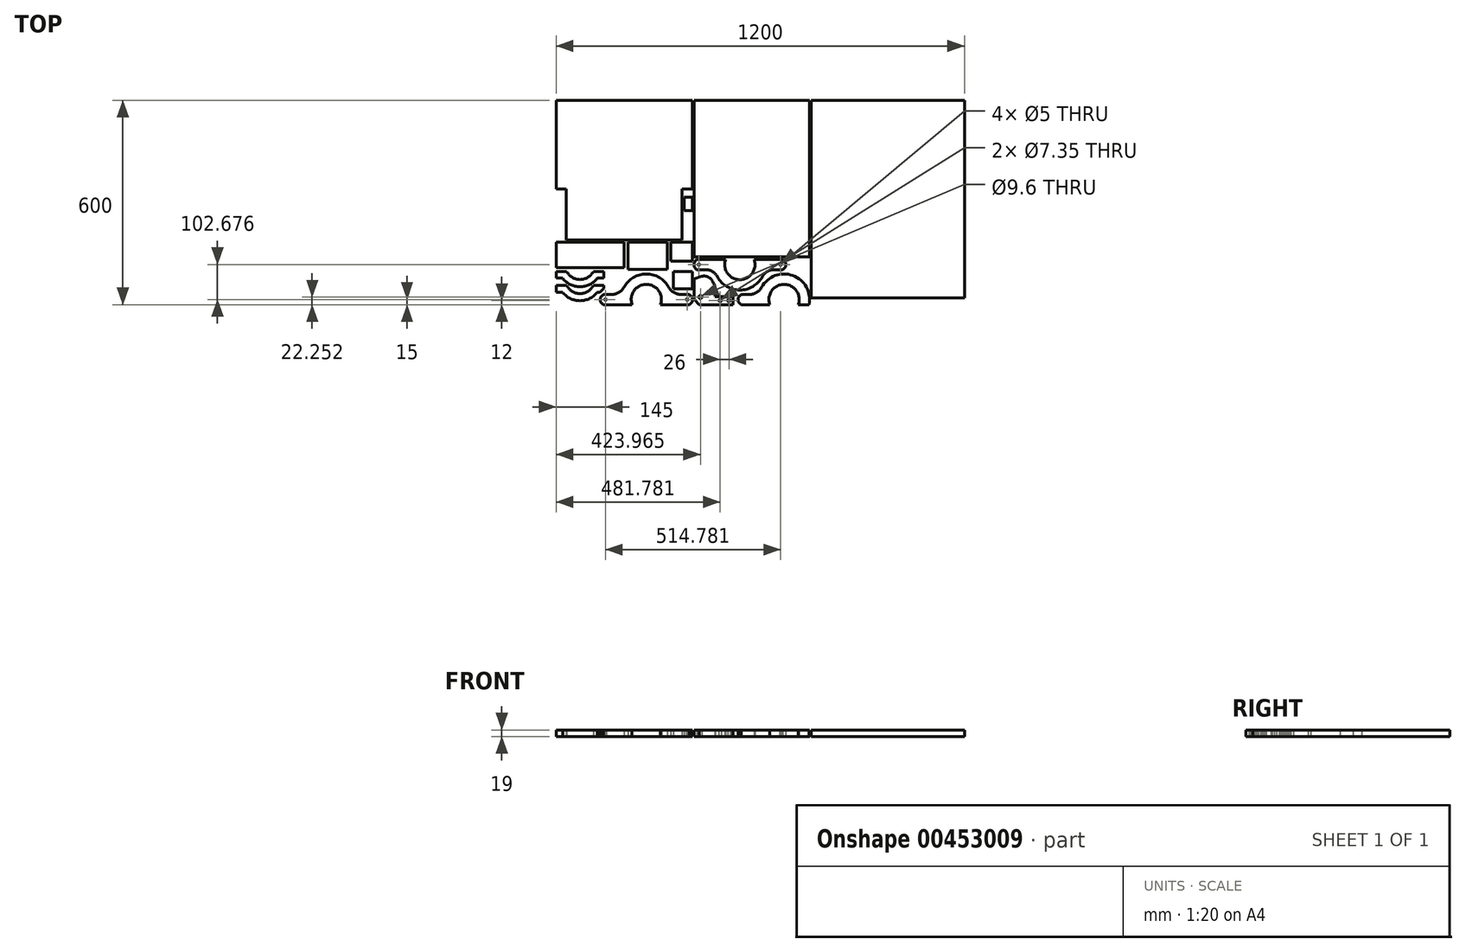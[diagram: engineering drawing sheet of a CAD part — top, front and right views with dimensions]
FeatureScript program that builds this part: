
annotation { "Feature Type Name" : "Feature", "Feature Type Description" : "" }
export const myFeature = defineFeature(function(context is Context, id is Id, definition is map)
    precondition{}
    {
        {
            var Q0;
            Q0=qCreatedBy(makeId("Top.planeOp"),FACE);
            var sketch = newSketch(context, id + "F0", { "sketchPlane" : qUnion([Q0])});
            skLineSegment(sketch, "E0", {"start": v(-600, 40) * mm, "end": v(-570, 40) * mm});
            skLineSegment(sketch, "E1", {"start": v(-570, 40) * mm, "end": v(-570, -110) * mm});
            skLineSegment(sketch, "E2", {"start": v(-570, -110) * mm, "end": v(-230, -110) * mm});
            skLineSegment(sketch, "E3", {"start": v(-230, -110) * mm, "end": v(-230, 40) * mm});
            skLineSegment(sketch, "E4", {"start": v(-230, 40) * mm, "end": v(-200, 40) * mm});
            skLineSegment(sketch, "E5", {"start": v(-200, 40) * mm, "end": v(-200, 300) * mm});
            skLineSegment(sketch, "E6", {"start": v(-200, 300) * mm, "end": v(-600, 300) * mm});
            skLineSegment(sketch, "E7", {"start": v(-600, 300) * mm, "end": v(-600, 40) * mm});
            skLineSegment(sketch, "E8", {"start": v(-400, -110) * mm, "end": v(-400, 300) * mm, "construction": true});
            skLineSegment(sketch, "E9.bottom", {"start": v(-600, 300) * mm, "end": v(600, 300) * mm, "construction": true});
            skLineSegment(sketch, "E9.top", {"start": v(-600, -300) * mm, "end": v(600, -300) * mm, "construction": true});
            skLineSegment(sketch, "E9.left", {"start": v(-600, 300) * mm, "end": v(-600, -300) * mm, "construction": true});
            skLineSegment(sketch, "E9.right", {"start": v(600, 300) * mm, "end": v(600, -300) * mm, "construction": true});
            skPoint(sketch, "E9.middle", {"position": v(0, 0) * mm});
            skLineSegment(sketch, "E10.bottom", {"start": v(-195.22, 300) * mm, "end": v(144.78, 300) * mm});
            skLineSegment(sketch, "E10.top", {"start": v(-195.22, -160) * mm, "end": v(144.78, -160) * mm});
            skLineSegment(sketch, "E10.left", {"start": v(-195.22, 300) * mm, "end": v(-195.22, -160) * mm});
            skLineSegment(sketch, "E10.right", {"start": v(144.78, 300) * mm, "end": v(144.78, -160) * mm});
            skLineSegment(sketch, "E11.bottom", {"start": v(600, 300) * mm, "end": v(150, 300) * mm});
            skLineSegment(sketch, "E11.top", {"start": v(600, -280) * mm, "end": v(150, -280) * mm});
            skLineSegment(sketch, "E11.left", {"start": v(600, 300) * mm, "end": v(600, -280) * mm});
            skLineSegment(sketch, "E11.right", {"start": v(150, 300) * mm, "end": v(150, -280) * mm});
            skSolve(sketch);
        }
        {
            var Q0;
            Q0=qCreatedBy(makeId("Top.planeOp"),FACE);
            var sketch = newSketch(context, id + "F1", { "sketchPlane" : qUnion([Q0])});
            skLineSegment(sketch, "E12.bottom", {"start": v(-600, -116.87) * mm, "end": v(-400, -116.87) * mm});
            skLineSegment(sketch, "E12.top", {"start": v(-600, -191.87) * mm, "end": v(-400, -191.87) * mm});
            skLineSegment(sketch, "E12.left", {"start": v(-600, -116.87) * mm, "end": v(-600, -191.87) * mm});
            skLineSegment(sketch, "E12.right", {"start": v(-400, -116.87) * mm, "end": v(-400, -191.87) * mm});
            skLineSegment(sketch, "E13.bottom", {"start": v(-388.52, -116.87) * mm, "end": v(-273.52, -116.87) * mm});
            skLineSegment(sketch, "E13.top", {"start": v(-388.52, -196.87) * mm, "end": v(-273.52, -196.87) * mm});
            skLineSegment(sketch, "E13.left", {"start": v(-388.52, -116.87) * mm, "end": v(-388.52, -196.87) * mm});
            skLineSegment(sketch, "E13.right", {"start": v(-273.52, -116.87) * mm, "end": v(-273.52, -196.87) * mm});
            skLineSegment(sketch, "E14.bottom", {"start": v(-263, -116.87) * mm, "end": v(-200, -116.87) * mm});
            skLineSegment(sketch, "E14.top", {"start": v(-263, -172.87) * mm, "end": v(-200, -172.87) * mm});
            skLineSegment(sketch, "E14.left", {"start": v(-263, -116.87) * mm, "end": v(-263, -172.87) * mm});
            skLineSegment(sketch, "E14.right", {"start": v(-200, -116.87) * mm, "end": v(-200, -172.87) * mm});
            skLineSegment(sketch, "E15.bottom", {"start": v(-223.55, 15.5) * mm, "end": v(-200, 15.5) * mm});
            skLineSegment(sketch, "E15.top", {"start": v(-223.55, -23.14) * mm, "end": v(-200, -23.14) * mm});
            skLineSegment(sketch, "E15.left", {"start": v(-223.55, 15.5) * mm, "end": v(-223.55, -23.14) * mm});
            skLineSegment(sketch, "E15.right", {"start": v(-200, 15.5) * mm, "end": v(-200, -23.14) * mm});
            skLineSegment(sketch, "E16", {"start": v(-470, -278.79) * mm, "end": v(-470, -291.21) * mm});
            skLineSegment(sketch, "E17", {"start": v(-470, -291.21) * mm, "end": v(-461.21, -300) * mm});
            skLineSegment(sketch, "E18", {"start": v(-461.21, -300) * mm, "end": v(-376.9, -300) * mm});
            skLineSegment(sketch, "E19", {"start": v(-470, -278.79) * mm, "end": v(-461.21, -270) * mm});
            skLineSegment(sketch, "E20", {"start": v(-461.21, -270) * mm, "end": v(-436, -270) * mm});
            skArc(sketch, "E21", {"start": v(-376.9, -300) * mm, "mid": v(-335, -240.5) * mm, "end": v(-293.1, -300) * mm});
            skLineSegment(sketch, "E22", {"start": v(-335, -285) * mm, "end": v(-335, -225.45) * mm, "construction": true});
            skLineSegment(sketch, "E23", {"start": v(-335, -285) * mm, "end": v(-470, -285) * mm, "construction": true});
            skCircle(sketch, "E24", {"center": v(-455, -285) * mm, "radius": 2.5 * mm});
            skArc(sketch, "E25", {"start": v(-436, -270) * mm, "mid": v(-415.57, -264.39) * mm, "end": v(-400.86, -249.13) * mm});
            skArc(sketch, "E26", {"start": v(-335, -210) * mm, "mid": v(-373.3, -220.52) * mm, "end": v(-400.86, -249.13) * mm});
            skLineSegment(sketch, "E27.MirrorCS", {"start": v(-200, -291.21) * mm, "end": v(-208.79, -300) * mm});
            skLineSegment(sketch, "E28.MirrorCS", {"start": v(-200, -278.79) * mm, "end": v(-200, -291.21) * mm});
            skLineSegment(sketch, "E29.MirrorCS", {"start": v(-208.79, -300) * mm, "end": v(-293.1, -300) * mm});
            skArc(sketch, "E30.MirrorCS", {"start": v(-234, -270) * mm, "mid": v(-254.43, -264.39) * mm, "end": v(-269.14, -249.13) * mm});
            skCircle(sketch, "E31.MirrorC", {"center": v(-215, -285) * mm, "radius": 2.5 * mm});
            skLineSegment(sketch, "E32.MirrorCS", {"start": v(-200, -278.79) * mm, "end": v(-208.79, -270) * mm});
            skLineSegment(sketch, "E33.MirrorCS", {"start": v(-208.79, -270) * mm, "end": v(-234, -270) * mm});
            skArc(sketch, "E34.MirrorCS", {"start": v(-335, -210) * mm, "mid": v(-296.7, -220.52) * mm, "end": v(-269.14, -249.13) * mm});
            skLineSegment(sketch, "E35.bottom", {"start": v(-200, -202.36) * mm, "end": v(-256, -202.36) * mm});
            skLineSegment(sketch, "E35.top", {"start": v(-200, -253.36) * mm, "end": v(-256, -253.36) * mm});
            skLineSegment(sketch, "E35.left", {"start": v(-200, -202.36) * mm, "end": v(-200, -253.36) * mm});
            skLineSegment(sketch, "E35.right", {"start": v(-256, -202.36) * mm, "end": v(-256, -253.36) * mm});
            skLineSegment(sketch, "E36", {"start": v(-569.2, -202.36) * mm, "end": v(-600, -202.36) * mm});
            skLineSegment(sketch, "E37", {"start": v(-600, -202.36) * mm, "end": v(-600, -222.36) * mm});
            skLineSegment(sketch, "E38", {"start": v(-600, -222.36) * mm, "end": v(-581.23, -222.36) * mm});
            skArc(sketch, "E39", {"start": v(-569.2, -202.36) * mm, "mid": v(-530, -226.36) * mm, "end": v(-490.8, -202.36) * mm});
            skArc(sketch, "E40", {"start": v(-581.23, -222.36) * mm, "mid": v(-530, -247.36) * mm, "end": v(-478.77, -222.36) * mm});
            skLineSegment(sketch, "E41", {"start": v(-530, -182.36) * mm, "end": v(-530, -247.36) * mm, "construction": true});
            skLineSegment(sketch, "E42.MirrorCS", {"start": v(-460, -222.36) * mm, "end": v(-478.77, -222.36) * mm});
            skLineSegment(sketch, "E43.MirrorCS", {"start": v(-490.8, -202.36) * mm, "end": v(-460, -202.36) * mm});
            skLineSegment(sketch, "E44.MirrorCS", {"start": v(-460, -202.36) * mm, "end": v(-460, -222.36) * mm});
            skLineSegment(sketch, "E45", {"start": v(-569.2, -243.57) * mm, "end": v(-600, -243.57) * mm});
            skLineSegment(sketch, "E46", {"start": v(-600, -243.57) * mm, "end": v(-600, -263.57) * mm});
            skLineSegment(sketch, "E47", {"start": v(-600, -263.57) * mm, "end": v(-581.23, -263.57) * mm});
            skArc(sketch, "E48", {"start": v(-569.2, -243.57) * mm, "mid": v(-530, -267.57) * mm, "end": v(-490.8, -243.57) * mm});
            skArc(sketch, "E49", {"start": v(-581.23, -263.57) * mm, "mid": v(-530, -288.57) * mm, "end": v(-478.77, -263.57) * mm});
            skLineSegment(sketch, "E50", {"start": v(-530, -223.57) * mm, "end": v(-530, -288.57) * mm, "construction": true});
            skLineSegment(sketch, "E51.MirrorCS", {"start": v(-471.72, -263.57) * mm, "end": v(-478.77, -263.57) * mm});
            skLineSegment(sketch, "E52.MirrorCS", {"start": v(-490.8, -243.57) * mm, "end": v(-460, -243.57) * mm});
            skLineSegment(sketch, "E53.MirrorCS", {"start": v(-460, -243.57) * mm, "end": v(-460, -251.85) * mm});
            skLineSegment(sketch, "E54", {"start": v(74.78, -188.54) * mm, "end": v(74.78, -176.11) * mm});
            skLineSegment(sketch, "E55", {"start": v(74.78, -176.11) * mm, "end": v(66, -167.32) * mm});
            skLineSegment(sketch, "E56", {"start": v(66, -167.32) * mm, "end": v(-18.32, -167.32) * mm});
            skLineSegment(sketch, "E57", {"start": v(74.78, -188.54) * mm, "end": v(66, -197.32) * mm});
            skLineSegment(sketch, "E58", {"start": v(66, -197.32) * mm, "end": v(40.78, -197.32) * mm});
            skArc(sketch, "E59", {"start": v(-18.32, -167.32) * mm, "mid": v(-60.22, -226.82) * mm, "end": v(-102.11, -167.32) * mm});
            skLineSegment(sketch, "E60", {"start": v(-60.22, -182.32) * mm, "end": v(-60.22, -241.87) * mm, "construction": true});
            skLineSegment(sketch, "E61", {"start": v(-60.22, -182.32) * mm, "end": v(74.78, -182.32) * mm, "construction": true});
            skCircle(sketch, "E62", {"center": v(59.78, -182.32) * mm, "radius": 2.5 * mm});
            skArc(sketch, "E63", {"start": v(40.78, -197.32) * mm, "mid": v(20.35, -202.94) * mm, "end": v(5.65, -218.2) * mm});
            skArc(sketch, "E64", {"start": v(-60.22, -257.32) * mm, "mid": v(-21.91, -246.8) * mm, "end": v(5.65, -218.2) * mm});
            skLineSegment(sketch, "E65.MirrorCS", {"start": v(-195.22, -176.11) * mm, "end": v(-186.43, -167.32) * mm});
            skLineSegment(sketch, "E66.MirrorCS", {"start": v(-195.22, -188.54) * mm, "end": v(-195.22, -176.11) * mm});
            skLineSegment(sketch, "E67.MirrorCS", {"start": v(-186.43, -167.32) * mm, "end": v(-102.11, -167.32) * mm});
            skArc(sketch, "E68.MirrorCS", {"start": v(-161.22, -197.32) * mm, "mid": v(-140.79, -202.94) * mm, "end": v(-126.08, -218.2) * mm});
            skCircle(sketch, "E69.MirrorC", {"center": v(-180.22, -182.32) * mm, "radius": 2.5 * mm});
            skLineSegment(sketch, "E70.MirrorCS", {"start": v(-195.22, -188.54) * mm, "end": v(-186.43, -197.32) * mm});
            skLineSegment(sketch, "E71.MirrorCS", {"start": v(-186.43, -197.32) * mm, "end": v(-161.22, -197.32) * mm});
            skArc(sketch, "E72.MirrorCS", {"start": v(-60.22, -257.32) * mm, "mid": v(-98.52, -246.8) * mm, "end": v(-126.08, -218.2) * mm});
            skLineSegment(sketch, "E73", {"start": v(-471.72, -263.57) * mm, "end": v(-460, -251.85) * mm});
            skPoint(sketch, "E74.orphan", {"position": v(-460, -263.57) * mm});
            skLineSegment(sketch, "E75", {"start": v(-31.22, -270) * mm, "end": v(-56.43, -270) * mm});
            skLineSegment(sketch, "E76", {"start": v(-56.43, -270) * mm, "end": v(-65.22, -278.79) * mm});
            skLineSegment(sketch, "E77", {"start": v(-65.22, -278.79) * mm, "end": v(-65.22, -291.21) * mm});
            skLineSegment(sketch, "E78", {"start": v(-65.22, -291.21) * mm, "end": v(-56.43, -300) * mm});
            skLineSegment(sketch, "E79", {"start": v(-56.43, -300) * mm, "end": v(27.89, -300) * mm});
            skLineSegment(sketch, "E80", {"start": v(-65.22, -285) * mm, "end": v(69.78, -285) * mm, "construction": true});
            skArc(sketch, "E81", {"start": v(27.89, -300) * mm, "mid": v(69.78, -240.5) * mm, "end": v(111.68, -300) * mm});
            skArc(sketch, "E82", {"start": v(-31.22, -270) * mm, "mid": v(-10.79, -264.39) * mm, "end": v(3.92, -249.13) * mm});
            skArc(sketch, "E83", {"start": v(143.27, -300) * mm, "mid": v(95.5, -214.55) * mm, "end": v(3.92, -249.13) * mm});
            skLineSegment(sketch, "E84", {"start": v(111.68, -300) * mm, "end": v(143.27, -300) * mm});
            skLineSegment(sketch, "E85", {"start": v(-179.84, -300) * mm, "end": v(-80.22, -300) * mm});
            skLineSegment(sketch, "E86", {"start": v(-80.22, -300) * mm, "end": v(-80.22, -276) * mm});
            skLineSegment(sketch, "E87", {"start": v(-80.22, -276) * mm, "end": v(-133.1, -276) * mm});
            skLineSegment(sketch, "E88", {"start": v(-195.22, -284.62) * mm, "end": v(-195.22, -225) * mm});
            skLineSegment(sketch, "E89", {"start": v(-195.22, -225) * mm, "end": v(-172.76, -217.18) * mm});
            skLineSegment(sketch, "E90", {"start": v(-195.22, -284.62) * mm, "end": v(-179.84, -300) * mm});
            skPoint(sketch, "E91.orphan", {"position": v(-195.22, -300) * mm});
            skEllipticalArc(sketch, "E92", {});
            skCircle(sketch, "E93", {"center": v(-92.22, -288) * mm, "radius": 3.67 * mm});
            skCircle(sketch, "E94", {"center": v(-118.22, -288) * mm, "radius": 3.67 * mm});
            skCircle(sketch, "E95", {"center": v(-176.03, -277.75) * mm, "radius": 4.8 * mm});
            const initialGuessF1  = {"E92": [-0.16490678446164297, -0.26298866367340085, 0, 1, 0.04715169966220856, 0.03310114752431062, 4.432814906983179, 0.23963872676930845]};
            skSetInitialGuess(sketch, initialGuessF1);
            skSolve(sketch);
        }
        {
            var Q0;
            Q0 = qSketchRegion(id + "F0", true);
            var Q1;
            Q1 = qSketchRegion(id + "F1", true);
            extrude(context, id + "F2", {"entities" : qUnion([Q0, Q1]), "depth" : 19 * mm});
        }
    });
